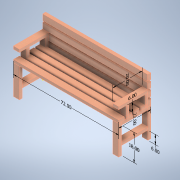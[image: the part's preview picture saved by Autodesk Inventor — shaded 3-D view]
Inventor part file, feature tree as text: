
AUTODESK INVENTOR PART (.ipt)
format: ipt  version: 2022 (Build 260153000, 153)  size: 258,048 bytes
history: native  units: in
note: dims shown in document units (in); Inventor stores cm internally (conversion verified against a paired STEP export)
features: sketch x8, other x7, extrude x6, pattern_linear x6
ambient origin geometry x8: Origin, YZ Plane, XZ Plane, XY Plane, X Axis, Y Axis, Z Axis, Center Point
bodies: Solid1 (feature_tree), Solid2 (feature_tree), Solid3 (feature_tree), Solid4 (feature_tree), Solid7 (feature_tree), Solid8 (feature_tree)
feature tree (27):
  other  "Annotations"
  extrude  "Extrusion1"  Depth=4.0in
  pattern_linear  "Rectangular Pattern1"  Count1=2 Spacing1=20.0in
  extrude  "Extrusion2"  Depth=6.0in
  pattern_linear  "Rectangular Pattern2"  Count1=2 Spacing1=68.0in
  sketch  "Sketch3"  dims[d10=2.0in d11=6.0in]
  sketch  "Sketch4"  dims[d12=1.0in d13=0.0in d14=0.7874in d16=68.0in]
  extrude  "Extrusion3"  Depth=4.0in
  pattern_linear  "Rectangular Pattern3"  Count1=4 Spacing1=5.0in
  extrude  "Extrusion4"  Depth=2.0in
  pattern_linear  "Rectangular Pattern4"  Count1=2 Spacing1=13.0in
  extrude  "Extrusion7"  Depth=2.0in TaperAngle=0.0deg
  pattern_linear  "Rectangular Pattern7"  Count1=2 Spacing1=68.0in
  extrude  "Extrusion8"  Depth=4.0in TaperAngle=0.0deg
  pattern_linear  "Rectangular Pattern8"  Count1=4 Spacing1=5.0in
  sketch  "Sketch1"  dims[d0=20.0in d1=4.0in]
  sketch  "Sketch2"  dims[d2=2.0in d3=0.0in d4=0.7874in d6=20.0in d7=0.7874in d9=68.0in]
  sketch  "Sketch5"  dims[d17=0.7874in d19=12.0in d20=4.0in]
  sketch  "Sketch6"  dims[d21=2.0in d22=0.0in d23=1.5748in d25=5.0in]
  sketch  "Sketch10"  dims[d26=2.0in d27=2.0in]
  sketch  "Sketch11"  dims[d28=8.0in d29=0.0in d30=0.7874in d32=13.0in d33=0.7874in d35=68.0in d49=2.0in d50=0.0in d51=0.7874in d53=68.0in d54=4.0in d55=0.0in d56=1.5748in d58=5.0in d59=18.0in d60=6.0in d61=22.0in d62=20.0in d63=0.0in d64=0.3937in d65=72.0in d66=0.0678in d67=6.0in d5=0.0344in d15=0.0344in]
  other  "Linear Dimension 1"
  other  "Linear Dimension 2"
  other  "Linear Dimension 3"
  other  "Linear Dimension 4"
  other  "Linear Dimension 5"
  other  "Linear Dimension 6"
